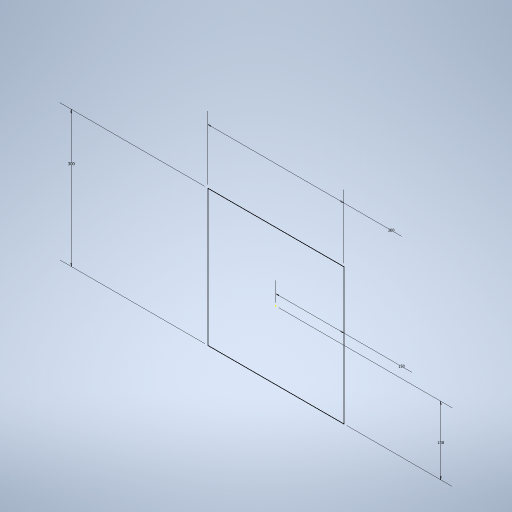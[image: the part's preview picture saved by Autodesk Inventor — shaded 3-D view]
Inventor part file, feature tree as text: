
AUTODESK INVENTOR PART (.ipt)
format: ipt  version: 2024 (Build 280153000, 153)  size: 233,984 bytes
history: native  units: mm
features: sketch x1
ambient origin geometry x8: Origin, YZ Plane, XZ Plane, XY Plane, X Axis, Y Axis, Z Axis, Center Point
feature tree (1):
  sketch  "Sketch1"  dims[d0=300.0mm d1=300.0mm d2=150.0mm d3=150.0mm]
